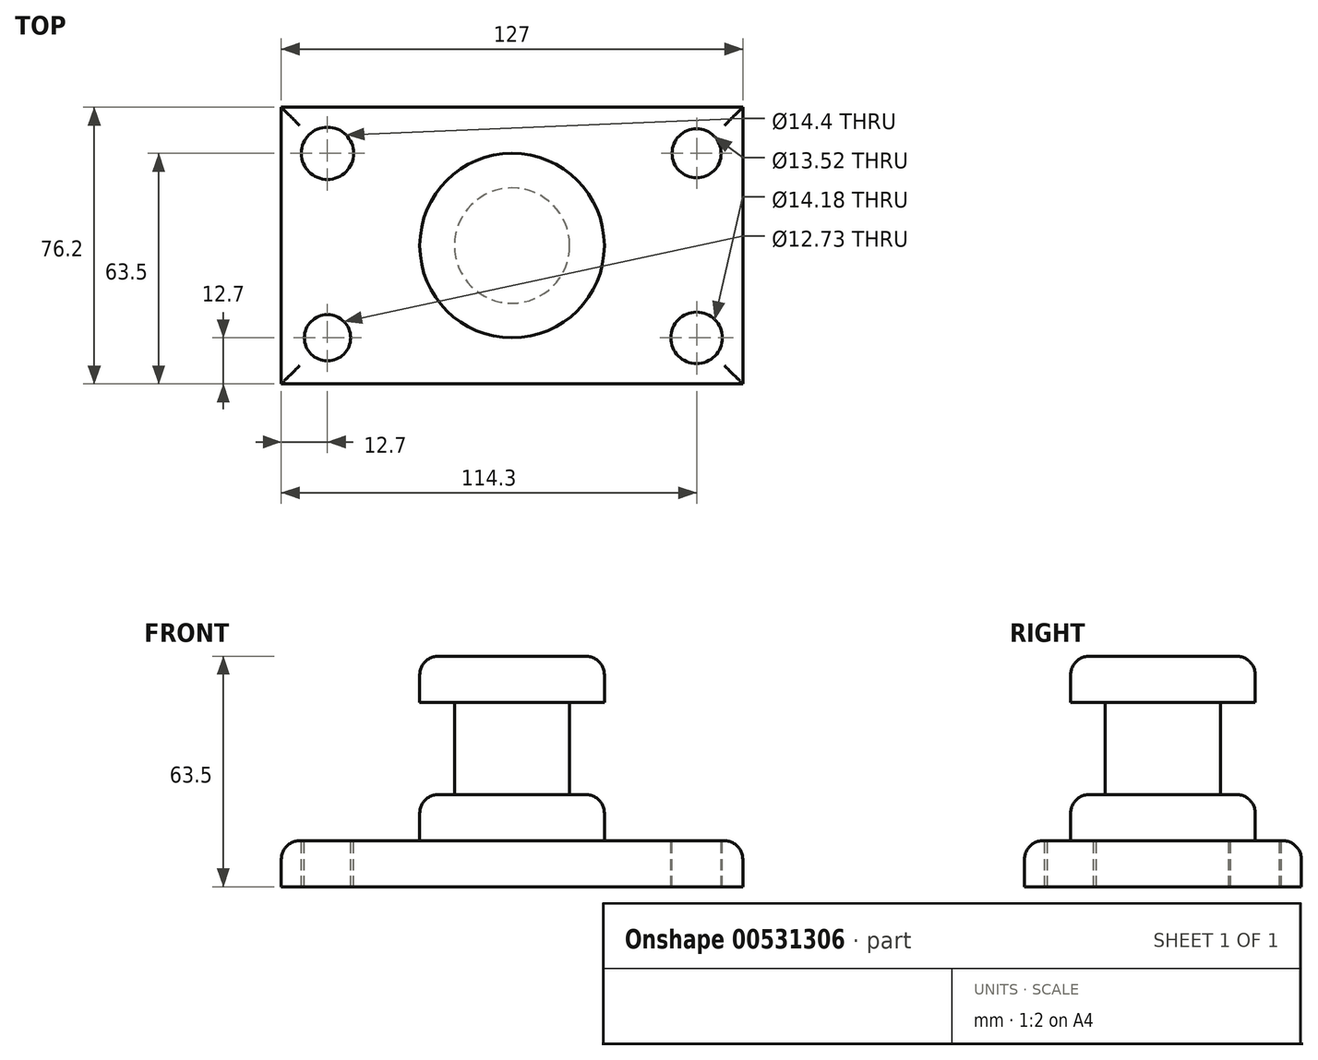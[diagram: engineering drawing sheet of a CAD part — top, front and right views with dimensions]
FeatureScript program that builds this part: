
annotation { "Feature Type Name" : "Feature", "Feature Type Description" : "" }
export const myFeature = defineFeature(function(context is Context, id is Id, definition is map)
    precondition{}
    {
        {
            var Q0;
            Q0=qCreatedBy(makeId("Top.planeOp"),FACE);
            var sketch = newSketch(context, id + "F0", { "sketchPlane" : qUnion([Q0])});
            skLineSegment(sketch, "E0.bottom", {"start": v(63.5, 38.1) * mm, "end": v(-63.5, 38.1) * mm});
            skLineSegment(sketch, "E0.top", {"start": v(63.5, -38.1) * mm, "end": v(-63.5, -38.1) * mm});
            skLineSegment(sketch, "E0.left", {"start": v(63.5, 38.1) * mm, "end": v(63.5, -38.1) * mm});
            skLineSegment(sketch, "E0.right", {"start": v(-63.5, 38.1) * mm, "end": v(-63.5, -38.1) * mm});
            skPoint(sketch, "E0.middle", {"position": v(0, 0) * mm});
            skSolve(sketch);
        }
        {
            var Q0;
            Q0=makeQuery(id+"F0.imprint","IMPRINT",FACE,{"disambiguationData":[TD([[makeQuery(id+"F0.imprint","IMPRINT",EDGE,{"derivedFrom":sQuery(id+"F0.wireOp",EDGE,"E0.bottom")}),1.0]])]});
            extrude(context, id + "F1", {"entities" : qUnion([Q0]), "depth" : 12.7 * mm, "offsetDistance" : 25.4 * mm});
        }
        {
            var Q0;
            Q0=makeQuery(id+"F1.opExtrude","CAP_FACE",FACE,{"disambiguationData":[OSD([sQuery(id+"F0.wireOp",EDGE,"E0.bottom"),sQuery(id+"F0.wireOp",EDGE,"E0.top"),sQuery(id+"F0.wireOp",EDGE,"E0.left"),sQuery(id+"F0.wireOp",EDGE,"E0.right")])],"isStart":false});
            var sketch = newSketch(context, id + "F2", { "sketchPlane" : qUnion([Q0])});
            skCircle(sketch, "E1", {"center": v(-50.8, 25.4) * mm, "radius": 7.2 * mm});
            skCircle(sketch, "E2", {"center": v(50.8, 25.4) * mm, "radius": 6.76 * mm});
            skCircle(sketch, "E3", {"center": v(-50.8, -25.4) * mm, "radius": 6.37 * mm});
            skCircle(sketch, "E4", {"center": v(50.8, -25.4) * mm, "radius": 7.1 * mm});
            skSolve(sketch);
        }
        {
            var Q0;
            Q0=makeQuery(id+"F2.imprint","IMPRINT",FACE,{"disambiguationData":[TD([[makeQuery(id+"F2.imprint","IMPRINT",EDGE,{"derivedFrom":sQuery(id+"F2.wireOp",EDGE,"E1")}),1.0]])]});
            var Q1;
            Q1=makeQuery(id+"F2.imprint","IMPRINT",FACE,{"disambiguationData":[TD([[makeQuery(id+"F2.imprint","IMPRINT",EDGE,{"derivedFrom":sQuery(id+"F2.wireOp",EDGE,"E2")}),1.0]])]});
            var Q2;
            Q2=makeQuery(id+"F2.imprint","IMPRINT",FACE,{"disambiguationData":[TD([[makeQuery(id+"F2.imprint","IMPRINT",EDGE,{"derivedFrom":sQuery(id+"F2.wireOp",EDGE,"E4")}),1.0]])]});
            var Q3;
            Q3=makeQuery(id+"F2.imprint","IMPRINT",FACE,{"disambiguationData":[TD([[makeQuery(id+"F2.imprint","IMPRINT",EDGE,{"derivedFrom":sQuery(id+"F2.wireOp",EDGE,"E3")}),1.0]])]});
            extrude(context, id + "F3", {"entities" : qUnion([Q0, Q1, Q2, Q3]), "operationType" : NewBodyOperationType.REMOVE, "endBound" : BoundingType.THROUGH_ALL, "oppositeDirection" : true, "depth" : 25.4 * mm, "offsetDistance" : 25.4 * mm});
        }
        {
            var Q0;
            Q0=qCreatedBy(makeId("Front.planeOp"),FACE);
            var sketch = newSketch(context, id + "F4", { "sketchPlane" : qUnion([Q0])});
            skLineSegment(sketch, "E5.bottom", {"start": v(0, 12.7) * mm, "end": v(25.4, 12.7) * mm});
            skLineSegment(sketch, "E5.top", {"start": v(0, 63.5) * mm, "end": v(25.4, 63.5) * mm});
            skLineSegment(sketch, "E5.left", {"start": v(0, 12.7) * mm, "end": v(0, 63.5) * mm});
            skLineSegment(sketch, "E5.right", {"start": v(25.4, 12.7) * mm, "end": v(25.4, 63.5) * mm});
            skSolve(sketch);
        }
        {
            var Q0;
            Q0=makeQuery(id+"F4.imprint","IMPRINT",FACE,{"disambiguationData":[TD([[makeQuery(id+"F4.imprint","IMPRINT",EDGE,{"derivedFrom":sQuery(id+"F4.wireOp",EDGE,"E5.bottom")}),1.0]])]});
            var Q1;
            Q1=sQuery(id+"F4.wireOp",EDGE,"E5.left");
            revolve(context, id + "F5", {"operationType" : NewBodyOperationType.ADD, "entities" : qUnion([Q0]), "axis" : qUnion([Q1]), "revolveType" : RevolveType.FULL});
        }
        {
            var Q0;
            Q0=qCreatedBy(makeId("Front.planeOp"),FACE);
            var sketch = newSketch(context, id + "F6", { "sketchPlane" : qUnion([Q0])});
            skLineSegment(sketch, "E6.bottom", {"start": v(15.87, 50.8) * mm, "end": v(36.5, 50.8) * mm});
            skLineSegment(sketch, "E6.top", {"start": v(15.87, 25.4) * mm, "end": v(36.5, 25.4) * mm});
            skLineSegment(sketch, "E6.left", {"start": v(15.87, 50.8) * mm, "end": v(15.87, 25.4) * mm});
            skLineSegment(sketch, "E6.right", {"start": v(36.5, 50.8) * mm, "end": v(36.5, 25.4) * mm});
            skSolve(sketch);
        }
        {
            var Q0;
            Q0=makeQuery(id+"F6.imprint","IMPRINT",FACE,{"disambiguationData":[TD([[makeQuery(id+"F6.imprint","IMPRINT",EDGE,{"derivedFrom":sQuery(id+"F6.wireOp",EDGE,"E6.bottom")}),-1.0]])]});
            var Q1;
            Q1=makeQuery(id+"F5.opRevolve","SWEPT_FACE",FACE,{"disambiguationData":[OSD([sQuery(id+"F4.wireOp",EDGE,"E5.right")])]});
            revolve(context, id + "F7", {"operationType" : NewBodyOperationType.REMOVE, "entities" : qUnion([Q0]), "axis" : qUnion([Q1]), "revolveType" : RevolveType.FULL, "oppositeDirection" : true});
        }
        {
            var Q0;
            Q0=makeQuery(id+"F5.opRevolve","SWEPT_EDGE",EDGE,{"disambiguationData":[OSD([sQuery(id+"F4.wireOp",EDGE,"E5.top"),sQuery(id+"F4.wireOp",EDGE,"E5.right")])]});
            var Q1;
            Q1=makeQuery(id+"F5.opRevolve","SWEPT_EDGE",EDGE,{"disambiguationData":[OSD([sQuery(id+"F4.wireOp",EDGE,"E5.bottom"),sQuery(id+"F4.wireOp",EDGE,"E5.right")])]});
            var Q2;
            Q2=makeQuery(id+"F7.boolean.opBoolean","INTERSECT",EDGE,{"derivedFrom":[makeQuery(id+"F5.opRevolve","SWEPT_FACE",FACE,{"disambiguationData":[OSD([sQuery(id+"F4.wireOp",EDGE,"E5.right")])]}),makeQuery(id+"F7.opRevolve","SWEPT_FACE",FACE,{"disambiguationData":[OSD([sQuery(id+"F6.wireOp",EDGE,"E6.top")])]})]});
            var Q3;
            Q3=makeQuery(id+"F1.opExtrude","CAP_EDGE",EDGE,{"disambiguationData":[OSD([sQuery(id+"F0.wireOp",EDGE,"E0.top")])],"isStart":false});
            var Q4;
            Q4=makeQuery(id+"F1.opExtrude","CAP_EDGE",EDGE,{"disambiguationData":[OSD([sQuery(id+"F0.wireOp",EDGE,"E0.left")])],"isStart":false});
            var Q5;
            Q5=makeQuery(id+"F1.opExtrude","CAP_EDGE",EDGE,{"disambiguationData":[OSD([sQuery(id+"F0.wireOp",EDGE,"E0.bottom")])],"isStart":false});
            var Q6;
            Q6=makeQuery(id+"F1.opExtrude","CAP_EDGE",EDGE,{"disambiguationData":[OSD([sQuery(id+"F0.wireOp",EDGE,"E0.right")])],"isStart":false});
            fillet(context, id + "F8", {"entities" : qUnion([Q0, Q1, Q2, Q3, Q4, Q5, Q6]), "radius" : 5.08 * mm, "tangentPropagation" : true, "allowEdgeOverflow" : false});
        }
    });
